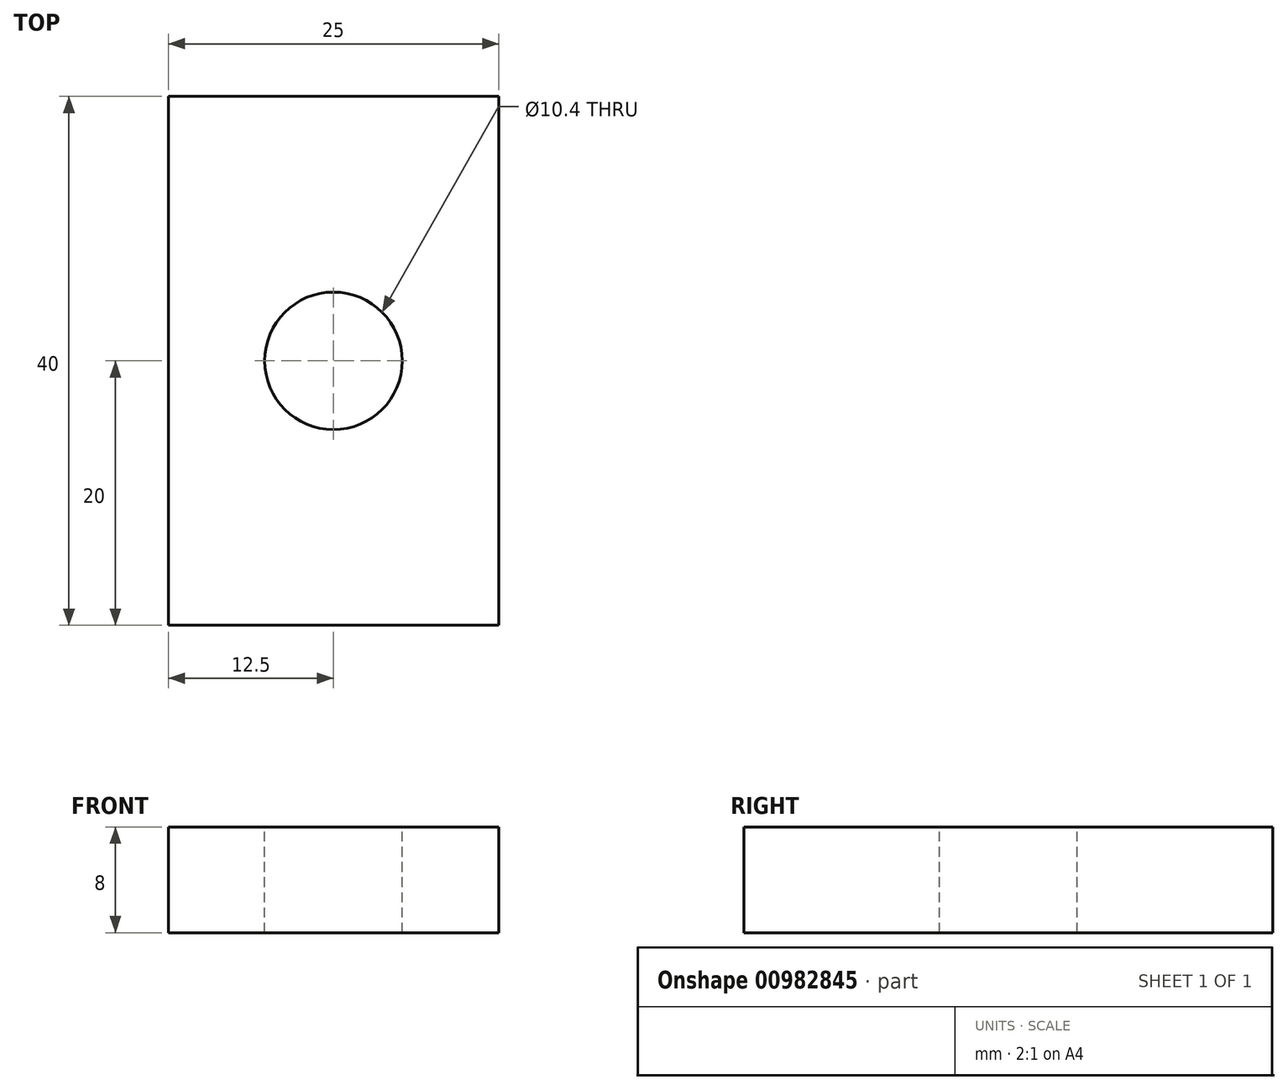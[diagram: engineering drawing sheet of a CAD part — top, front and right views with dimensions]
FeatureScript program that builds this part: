
annotation { "Feature Type Name" : "Feature", "Feature Type Description" : "" }
export const myFeature = defineFeature(function(context is Context, id is Id, definition is map)
    precondition{}
    {
        {
            var Q0;
            Q0=qCreatedBy(makeId("Front.planeOp"),FACE);
            var sketch = newSketch(context, id + "F0", { "sketchPlane" : qUnion([Q0])});
            skLineSegment(sketch, "E0.bottom", {"start": v(-12.5, -4) * mm, "end": v(12.5, -4) * mm});
            skLineSegment(sketch, "E0.top", {"start": v(-12.5, 4) * mm, "end": v(12.5, 4) * mm});
            skLineSegment(sketch, "E0.left", {"start": v(-12.5, -4) * mm, "end": v(-12.5, 4) * mm});
            skLineSegment(sketch, "E0.right", {"start": v(12.5, -4) * mm, "end": v(12.5, 4) * mm});
            skPoint(sketch, "E0.middle", {"position": v(0, 0) * mm});
            skSolve(sketch);
        }
        {
            var Q0;
            Q0 = qSketchRegion(id + "F0", true);
            extrude(context, id + "F1", {"entities" : qUnion([Q0]), "depth" : 40 * mm, "offsetDistance" : 25 * mm});
        }
        {
            var Q0;
            Q0=makeQuery(id+"F1.opExtrude","SWEPT_FACE",FACE,{"disambiguationData":[OSD([sQuery(id+"F0.wireOp",EDGE,"E0.top")])]});
            var sketch = newSketch(context, id + "F2", { "sketchPlane" : qUnion([Q0])});
            skCircle(sketch, "E1", {"center": v(0, -20) * mm, "radius": 5.2 * mm});
            skPoint(sketch, "E1.centerSnap0", {"position": v(12.5, -20) * mm});
            skSolve(sketch);
        }
        {
            var Q0;
            Q0 = qSketchRegion(id + "F2", true);
            extrude(context, id + "F3", {"entities" : qUnion([Q0]), "operationType" : NewBodyOperationType.REMOVE, "oppositeDirection" : true, "depth" : 25 * mm, "offsetDistance" : 25 * mm});
        }
    });
